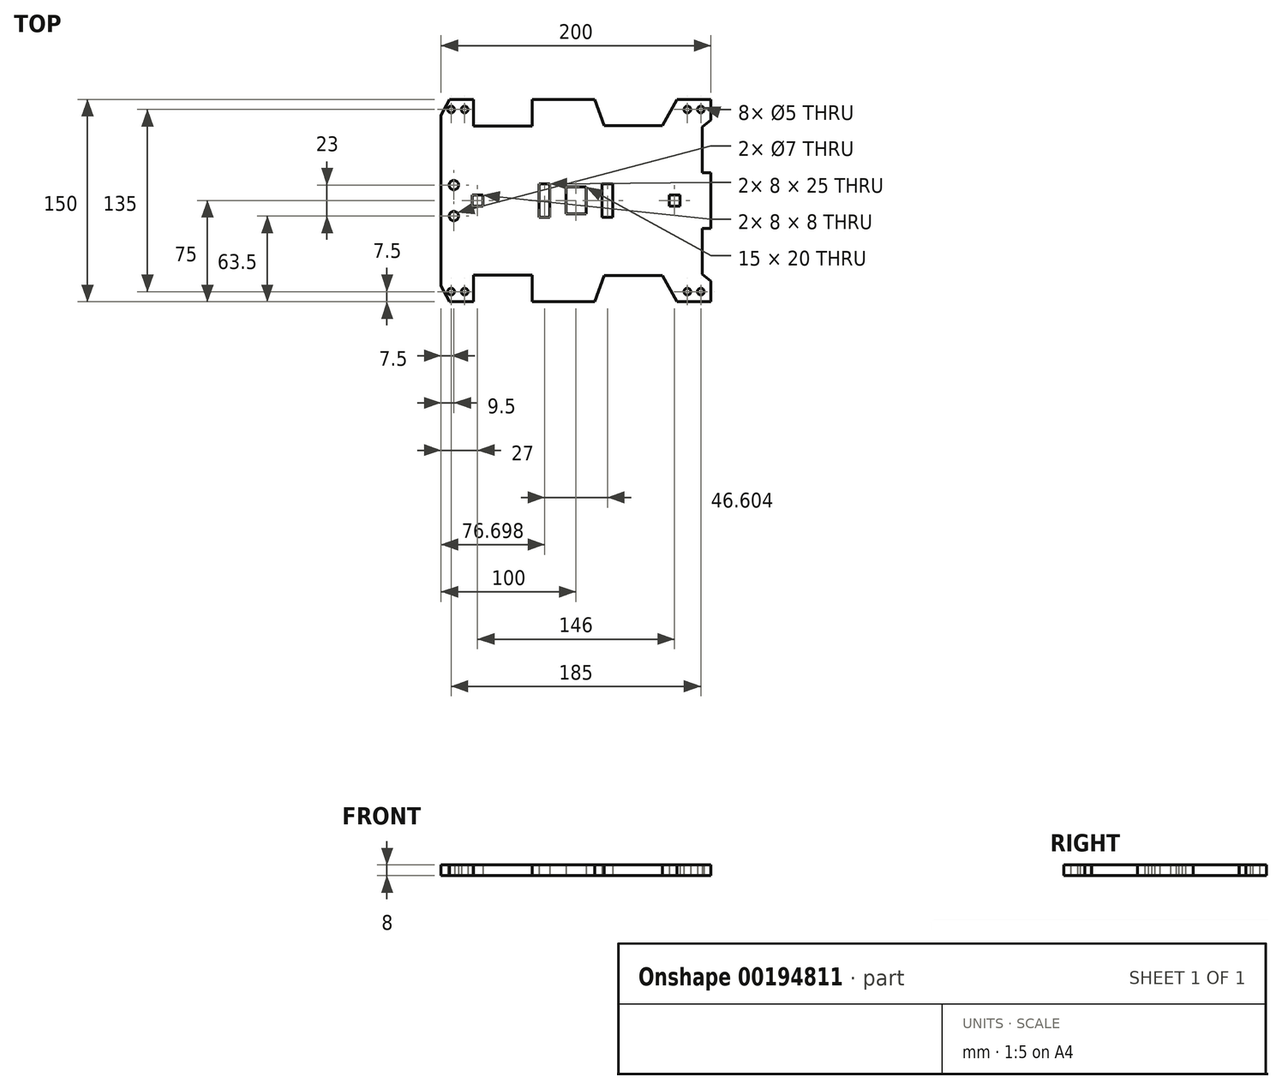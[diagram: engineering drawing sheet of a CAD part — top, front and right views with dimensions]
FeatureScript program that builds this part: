
annotation { "Feature Type Name" : "Feature", "Feature Type Description" : "" }
export const myFeature = defineFeature(function(context is Context, id is Id, definition is map)
    precondition{}
    {
        {
            var Q0;
            Q0=qCreatedBy(makeId("Top.planeOp"),FACE);
            var sketch = newSketch(context, id + "F0", { "sketchPlane" : qUnion([Q0])});
            skLineSegment(sketch, "E0.bottom", {"start": v(-100, 75) * mm, "end": v(100, 75) * mm});
            skLineSegment(sketch, "E0.top", {"start": v(-100, -75) * mm, "end": v(100, -75) * mm});
            skLineSegment(sketch, "E0.left", {"start": v(-100, 75) * mm, "end": v(-100, -75) * mm});
            skLineSegment(sketch, "E0.right", {"start": v(100, 75) * mm, "end": v(100, -75) * mm});
            skPoint(sketch, "E0.middle", {"position": v(0, 0) * mm});
            skLineSegment(sketch, "E1.bottom", {"start": v(-27.3, 12.5) * mm, "end": v(-19.3, 12.5) * mm});
            skLineSegment(sketch, "E1.top", {"start": v(-27.3, -12.5) * mm, "end": v(-19.3, -12.5) * mm});
            skLineSegment(sketch, "E1.left", {"start": v(-27.3, 12.5) * mm, "end": v(-27.3, -12.5) * mm});
            skLineSegment(sketch, "E1.right", {"start": v(-19.3, 12.5) * mm, "end": v(-19.3, -12.5) * mm});
            skPoint(sketch, "E1.middle", {"position": v(-23.3, 0) * mm});
            skLineSegment(sketch, "E2.MirrorCS", {"start": v(19.3, 12.5) * mm, "end": v(19.3, -12.5) * mm});
            skLineSegment(sketch, "E3.MirrorCS", {"start": v(27.3, 12.5) * mm, "end": v(27.3, -12.5) * mm});
            skLineSegment(sketch, "E4.MirrorCS", {"start": v(27.3, -12.5) * mm, "end": v(19.3, -12.5) * mm});
            skLineSegment(sketch, "E5.MirrorCS", {"start": v(27.3, 12.5) * mm, "end": v(19.3, 12.5) * mm});
            skPoint(sketch, "E6.MirrorP", {"position": v(23.3, 0) * mm});
            skLineSegment(sketch, "E7.bottom", {"start": v(-7.5, 10) * mm, "end": v(7.5, 10) * mm});
            skLineSegment(sketch, "E7.top", {"start": v(-7.5, -10) * mm, "end": v(7.5, -10) * mm});
            skLineSegment(sketch, "E7.left", {"start": v(-7.5, 10) * mm, "end": v(-7.5, -10) * mm});
            skLineSegment(sketch, "E7.right", {"start": v(7.5, 10) * mm, "end": v(7.5, -10) * mm});
            skCircle(sketch, "E8", {"center": v(-92.5, 67.5) * mm, "radius": 2.5 * mm});
            skCircle(sketch, "E9", {"center": v(-82.5, 67.5) * mm, "radius": 2.5 * mm});
            skCircle(sketch, "E10.MirrorC", {"center": v(82.5, 67.5) * mm, "radius": 2.5 * mm});
            skCircle(sketch, "E11.MirrorC", {"center": v(92.5, 67.5) * mm, "radius": 2.5 * mm});
            skCircle(sketch, "E12.MirrorC", {"center": v(-92.5, -67.5) * mm, "radius": 2.5 * mm});
            skCircle(sketch, "E13.MirrorC", {"center": v(-82.5, -67.5) * mm, "radius": 2.5 * mm});
            skCircle(sketch, "E14.MirrorC", {"center": v(82.5, -67.5) * mm, "radius": 2.5 * mm});
            skCircle(sketch, "E15.MirrorC", {"center": v(92.5, -67.5) * mm, "radius": 2.5 * mm});
            skPoint(sketch, "E16", {"position": v(-7.5, 0) * mm});
            skCircle(sketch, "E17", {"center": v(-90.5, 11.5) * mm, "radius": 3.5 * mm});
            skCircle(sketch, "E18.MirrorC", {"center": v(-90.5, -11.5) * mm, "radius": 3.5 * mm});
            skLineSegment(sketch, "E19.bottom", {"start": v(-77, 4) * mm, "end": v(-69, 4) * mm});
            skLineSegment(sketch, "E19.top", {"start": v(-77, -4) * mm, "end": v(-69, -4) * mm});
            skLineSegment(sketch, "E19.left", {"start": v(-77, 4) * mm, "end": v(-77, -4) * mm});
            skLineSegment(sketch, "E19.right", {"start": v(-69, 4) * mm, "end": v(-69, -4) * mm});
            skPoint(sketch, "E19.middle", {"position": v(-73, 0) * mm});
            skLineSegment(sketch, "E20.MirrorCS", {"start": v(69, 4) * mm, "end": v(69, -4) * mm});
            skLineSegment(sketch, "E21.MirrorCS", {"start": v(77, 4) * mm, "end": v(69, 4) * mm});
            skLineSegment(sketch, "E22.MirrorCS", {"start": v(77, -4) * mm, "end": v(69, -4) * mm});
            skLineSegment(sketch, "E23.MirrorCS", {"start": v(77, 4) * mm, "end": v(77, -4) * mm});
            skPoint(sketch, "E24.MirrorP", {"position": v(73, 0) * mm});
            skLineSegment(sketch, "E25", {"start": v(-100, -63.03) * mm, "end": v(-93.77, -75) * mm});
            skLineSegment(sketch, "E26", {"start": v(-76.08, -75) * mm, "end": v(-76.08, -55.17) * mm});
            skLineSegment(sketch, "E27", {"start": v(-76.08, -55.17) * mm, "end": v(-32.57, -55.17) * mm});
            skLineSegment(sketch, "E28", {"start": v(-32.57, -55.17) * mm, "end": v(-32.57, -75) * mm});
            skLineSegment(sketch, "E29", {"start": v(74.96, -75) * mm, "end": v(64.01, -55.45) * mm});
            skLineSegment(sketch, "E30", {"start": v(64.01, -55.45) * mm, "end": v(20.78, -55.45) * mm});
            skLineSegment(sketch, "E31", {"start": v(20.78, -55.45) * mm, "end": v(13.76, -75) * mm});
            skLineSegment(sketch, "E32.MirrorCS", {"start": v(-76.08, 55.17) * mm, "end": v(-32.57, 55.17) * mm});
            skLineSegment(sketch, "E33.MirrorCS", {"start": v(-32.57, 55.17) * mm, "end": v(-32.57, 75) * mm});
            skLineSegment(sketch, "E34.MirrorCS", {"start": v(-76.08, 75) * mm, "end": v(-76.08, 55.17) * mm});
            skLineSegment(sketch, "E35.MirrorCS", {"start": v(20.78, 55.45) * mm, "end": v(13.76, 75) * mm});
            skLineSegment(sketch, "E36.MirrorCS", {"start": v(64.01, 55.45) * mm, "end": v(20.78, 55.45) * mm});
            skLineSegment(sketch, "E37.MirrorCS", {"start": v(74.96, 75) * mm, "end": v(64.01, 55.45) * mm});
            skLineSegment(sketch, "E38.MirrorCS", {"start": v(-100, 63.03) * mm, "end": v(-93.77, 75) * mm});
            skLineSegment(sketch, "E39", {"start": v(100, 59.66) * mm, "end": v(93.49, 54.6) * mm});
            skLineSegment(sketch, "E40", {"start": v(93.49, 54.6) * mm, "end": v(93.49, 20.64) * mm});
            skLineSegment(sketch, "E41", {"start": v(93.49, 20.64) * mm, "end": v(100, 20.64) * mm});
            skLineSegment(sketch, "E42.MirrorCS", {"start": v(93.49, -20.64) * mm, "end": v(100, -20.64) * mm});
            skLineSegment(sketch, "E43.MirrorCS", {"start": v(93.49, -54.6) * mm, "end": v(93.49, -20.64) * mm});
            skLineSegment(sketch, "E44.MirrorCS", {"start": v(100, -59.66) * mm, "end": v(93.49, -54.6) * mm});
            skSolve(sketch);
        }
        {
            var Q0;
            Q0=makeQuery(id+"F0.imprint","IMPRINT",FACE,{"disambiguationData":[TD([[makeQuery(id+"F0.imprint","IMPRINT",EDGE,{"derivedFrom":sQuery(id+"F0.wireOp",EDGE,"E0.bottom")}),-1.0]])]});
            extrude(context, id + "F1", {"entities" : qUnion([Q0]), "depth" : 8 * mm});
        }
    });
